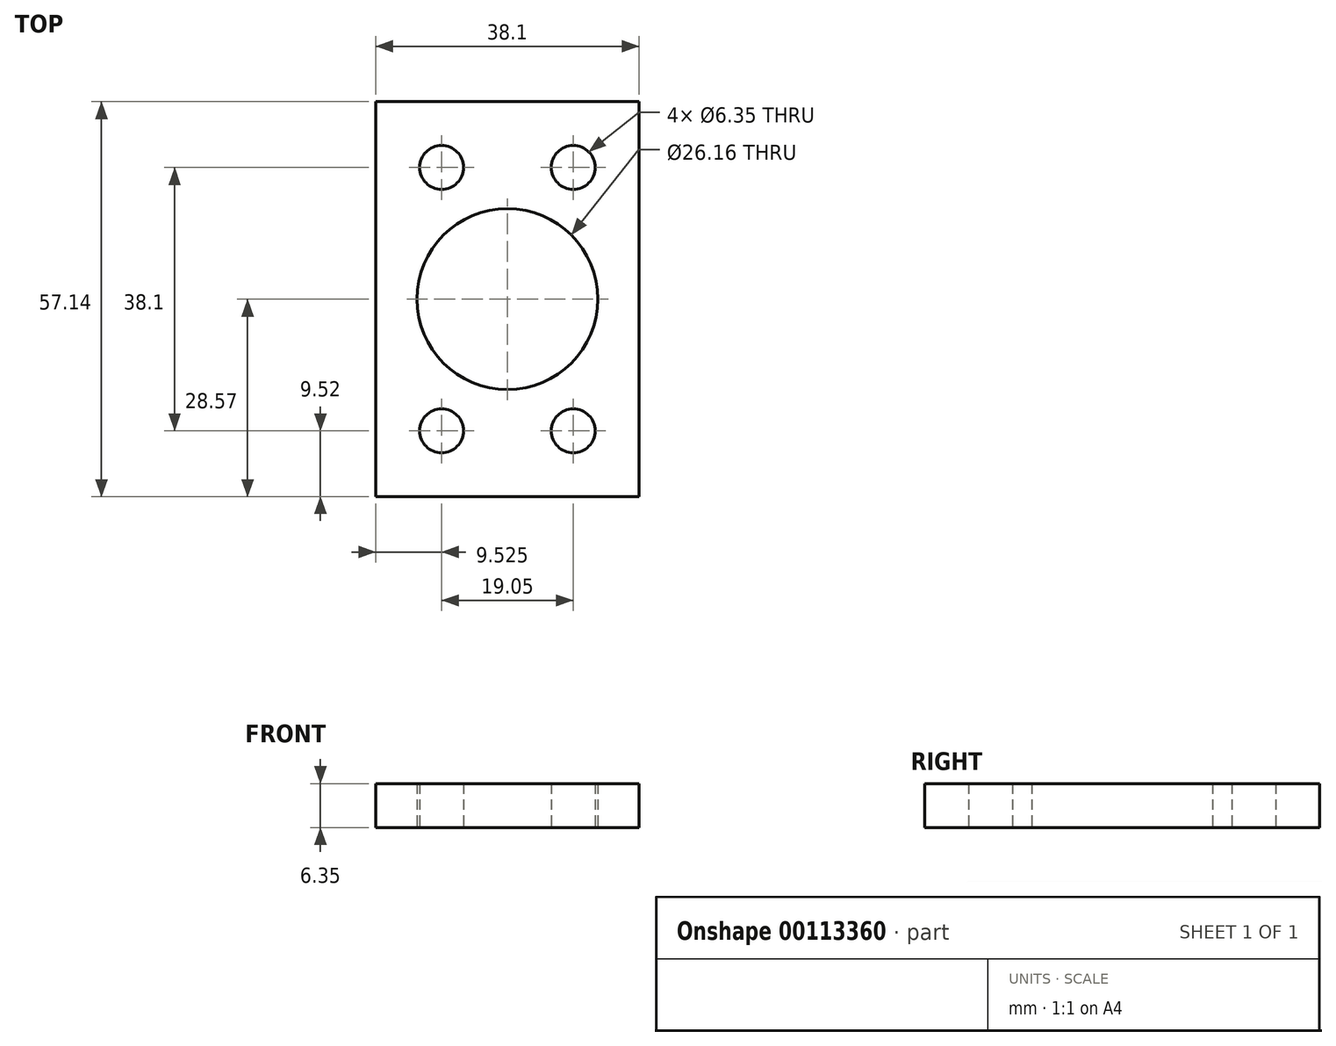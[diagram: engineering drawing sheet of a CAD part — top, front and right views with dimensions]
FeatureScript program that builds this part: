
annotation { "Feature Type Name" : "Feature", "Feature Type Description" : "" }
export const myFeature = defineFeature(function(context is Context, id is Id, definition is map)
    precondition{}
    {
        {
            var Q0;
            Q0=qCreatedBy(makeId("Top.planeOp"),FACE);
            var sketch = newSketch(context, id + "F0", { "sketchPlane" : qUnion([Q0])});
            skLineSegment(sketch, "E0.bottom", {"start": v(19.05, 28.58) * mm, "end": v(-19.05, 28.57) * mm});
            skLineSegment(sketch, "E0.top", {"start": v(19.05, -28.57) * mm, "end": v(-19.05, -28.58) * mm});
            skLineSegment(sketch, "E0.left", {"start": v(19.05, 28.58) * mm, "end": v(19.05, -28.57) * mm});
            skLineSegment(sketch, "E0.right", {"start": v(-19.05, 28.58) * mm, "end": v(-19.05, -28.58) * mm});
            skPoint(sketch, "E0.middle", {"position": v(0, 0) * mm});
            skCircle(sketch, "E1", {"center": v(0, 0) * mm, "radius": 13.08 * mm});
            skLineSegment(sketch, "E2", {"start": v(-9.53, 28.58) * mm, "end": v(-9.53, -28.58) * mm, "construction": true});
            skLineSegment(sketch, "E3", {"start": v(9.52, 28.57) * mm, "end": v(9.53, -28.58) * mm, "construction": true});
            skLineSegment(sketch, "E4", {"start": v(-19.05, 19.05) * mm, "end": v(19.05, 19.05) * mm, "construction": true});
            skLineSegment(sketch, "E5", {"start": v(-19.05, -19.05) * mm, "end": v(19.05, -19.05) * mm, "construction": true});
            skCircle(sketch, "E6", {"center": v(-9.53, 19.05) * mm, "radius": 3.18 * mm});
            skCircle(sketch, "E7", {"center": v(9.53, 19.05) * mm, "radius": 3.18 * mm});
            skCircle(sketch, "E8", {"center": v(-9.53, -19.05) * mm, "radius": 3.18 * mm});
            skCircle(sketch, "E9", {"center": v(9.53, -19.05) * mm, "radius": 3.18 * mm});
            skSolve(sketch);
        }
        {
            var Q0;
            Q0=makeQuery(id+"F0.imprint","IMPRINT",FACE,{"disambiguationData":[TD([[makeQuery(id+"F0.imprint","IMPRINT",EDGE,{"derivedFrom":sQuery(id+"F0.wireOp",EDGE,"E0.bottom")}),1.0]])]});
            extrude(context, id + "F1", {"entities" : qUnion([Q0]), "depth" : 6.35 * mm});
        }
    });
